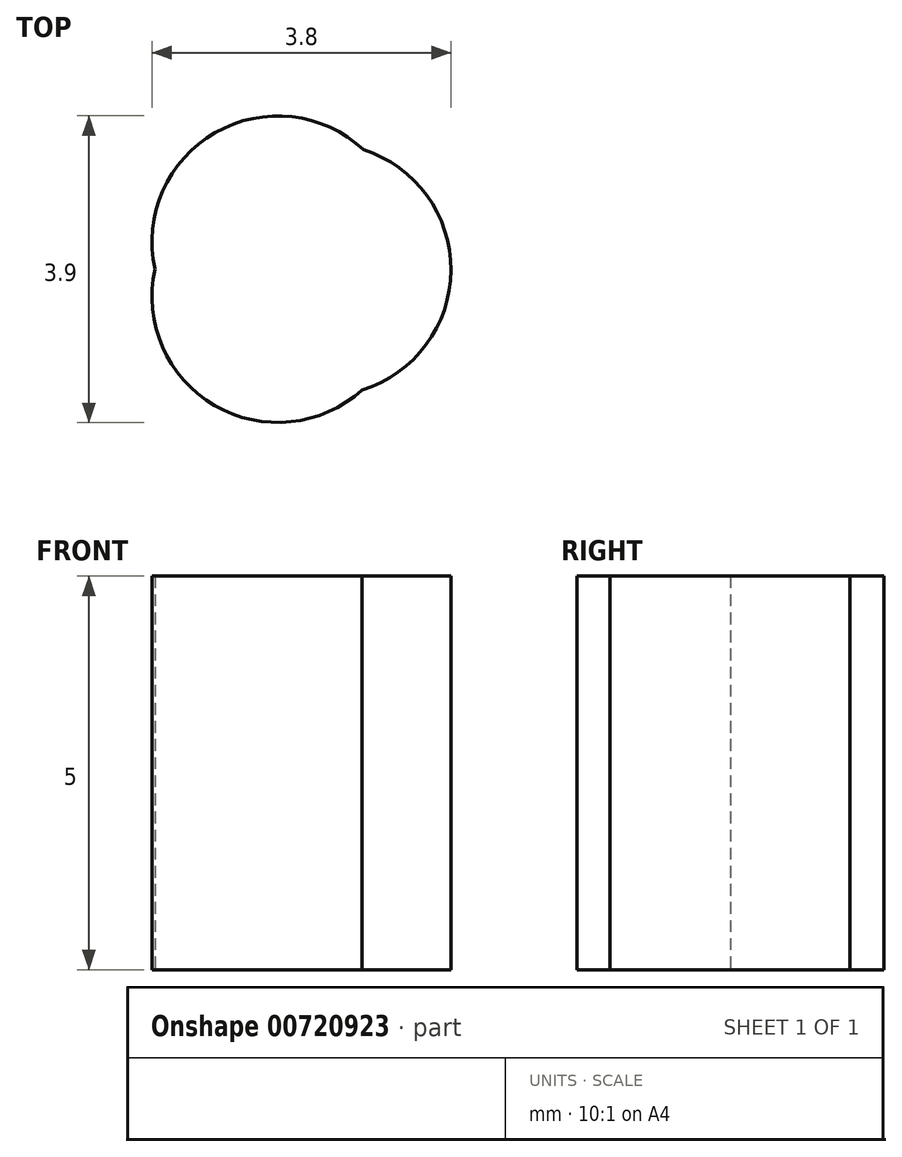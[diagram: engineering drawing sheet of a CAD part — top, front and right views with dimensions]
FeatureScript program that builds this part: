
annotation { "Feature Type Name" : "Feature", "Feature Type Description" : "" }
export const myFeature = defineFeature(function(context is Context, id is Id, definition is map)
    precondition{}
    {
        {
            var Q0;
            Q0=qCreatedBy(makeId("Top.planeOp"),FACE);
            var sketch = newSketch(context, id + "F0", { "sketchPlane" : qUnion([Q0])});
            skCircle(sketch, "E0", {"center": v(0.4, 0) * mm, "radius": 1.6 * mm});
            skCircle(sketch, "E1", {"center": v(-0.2, 0.35) * mm, "radius": 1.6 * mm});
            skCircle(sketch, "E2", {"center": v(-0.2, -0.35) * mm, "radius": 1.6 * mm});
            skSolve(sketch);
        }
        {
            var Q0;
            {var subQ0=sQuery(id+"F0.wireOp",EDGE,"E1");var subQ1=sQuery(id+"F0.wireOp",EDGE,"E0");var subQ2=makeQuery(id+"F0.imprint","INTERSECT",VERTEX,{"disambiguationData":[OD(0.0)],"derivedFrom":[subQ1,subQ0]});Q0=makeQuery(id+"F0.imprint","IMPRINT",FACE,{"disambiguationData":[TD([[makeQuery(id+"F0.imprint","IMPRINT",EDGE,{"disambiguationData":[TD([[subQ2,-1.0]])],"derivedFrom":subQ1}),-1.0]])]});}
            var Q1;
            {var subQ0=sQuery(id+"F0.wireOp",EDGE,"E1");var subQ1=sQuery(id+"F0.wireOp",EDGE,"E0");var subQ2=makeQuery(id+"F0.imprint","INTERSECT",VERTEX,{"disambiguationData":[OD(0.0)],"derivedFrom":[subQ1,subQ0]});Q1=makeQuery(id+"F0.imprint","IMPRINT",FACE,{"disambiguationData":[TD([[makeQuery(id+"F0.imprint","IMPRINT",EDGE,{"disambiguationData":[TD([[subQ2,1.0]])],"derivedFrom":subQ1}),1.0]])]});}
            var Q2;
            {var subQ0=sQuery(id+"F0.wireOp",EDGE,"E2");var subQ1=sQuery(id+"F0.wireOp",EDGE,"E0");var subQ2=makeQuery(id+"F0.imprint","INTERSECT",VERTEX,{"disambiguationData":[OD(0.0)],"derivedFrom":[subQ1,subQ0]});Q2=makeQuery(id+"F0.imprint","IMPRINT",FACE,{"disambiguationData":[TD([[makeQuery(id+"F0.imprint","IMPRINT",EDGE,{"disambiguationData":[TD([[subQ2,1.0]])],"derivedFrom":subQ1}),-1.0]])]});}
            var Q3;
            {var subQ0=sQuery(id+"F0.wireOp",EDGE,"E1");var subQ1=sQuery(id+"F0.wireOp",EDGE,"E0");var subQ2=makeQuery(id+"F0.imprint","INTERSECT",VERTEX,{"disambiguationData":[OD(0.0)],"derivedFrom":[subQ1,subQ0]});Q3=makeQuery(id+"F0.imprint","IMPRINT",FACE,{"disambiguationData":[TD([[makeQuery(id+"F0.imprint","IMPRINT",EDGE,{"disambiguationData":[TD([[subQ2,-1.0]])],"derivedFrom":subQ1}),1.0]])]});}
            var Q4;
            {var subQ0=sQuery(id+"F0.wireOp",EDGE,"E2");var subQ1=sQuery(id+"F0.wireOp",EDGE,"E0");var subQ2=makeQuery(id+"F0.imprint","INTERSECT",VERTEX,{"disambiguationData":[OD(1.0)],"derivedFrom":[subQ1,subQ0]});Q4=makeQuery(id+"F0.imprint","IMPRINT",FACE,{"disambiguationData":[TD([[makeQuery(id+"F0.imprint","IMPRINT",EDGE,{"disambiguationData":[TD([[subQ2,-1.0]])],"derivedFrom":subQ1}),1.0]])]});}
            var Q5;
            {var subQ0=sQuery(id+"F0.wireOp",EDGE,"E2");var subQ1=sQuery(id+"F0.wireOp",EDGE,"E0");var subQ2=makeQuery(id+"F0.imprint","INTERSECT",VERTEX,{"disambiguationData":[OD(1.0)],"derivedFrom":[subQ1,subQ0]});Q5=makeQuery(id+"F0.imprint","IMPRINT",FACE,{"disambiguationData":[TD([[makeQuery(id+"F0.imprint","IMPRINT",EDGE,{"disambiguationData":[TD([[subQ2,-1.0]])],"derivedFrom":subQ1}),-1.0]])]});}
            var Q6;
            {var subQ0=sQuery(id+"F0.wireOp",EDGE,"E2");var subQ1=sQuery(id+"F0.wireOp",EDGE,"E0");var subQ2=makeQuery(id+"F0.imprint","INTERSECT",VERTEX,{"disambiguationData":[OD(0.0)],"derivedFrom":[subQ1,subQ0]});Q6=makeQuery(id+"F0.imprint","IMPRINT",FACE,{"disambiguationData":[TD([[makeQuery(id+"F0.imprint","IMPRINT",EDGE,{"disambiguationData":[TD([[subQ2,1.0]])],"derivedFrom":subQ1}),1.0]])]});}
            var Q7;
            Q7=sQuery(id+"F0.wireOp",EDGE,"E1");
            var Q8;
            Q8=sQuery(id+"F0.wireOp",EDGE,"E0");
            var Q9;
            Q9=sQuery(id+"F0.wireOp",EDGE,"E2");
            extrude(context, id + "F1", {"entities" : qUnion([Q0, Q1, Q2, Q3, Q4, Q5, Q6]), "surfaceEntities" : qUnion([Q7, Q8, Q9]), "depth" : 5 * mm, "offsetDistance" : 25 * mm});
        }
    });
